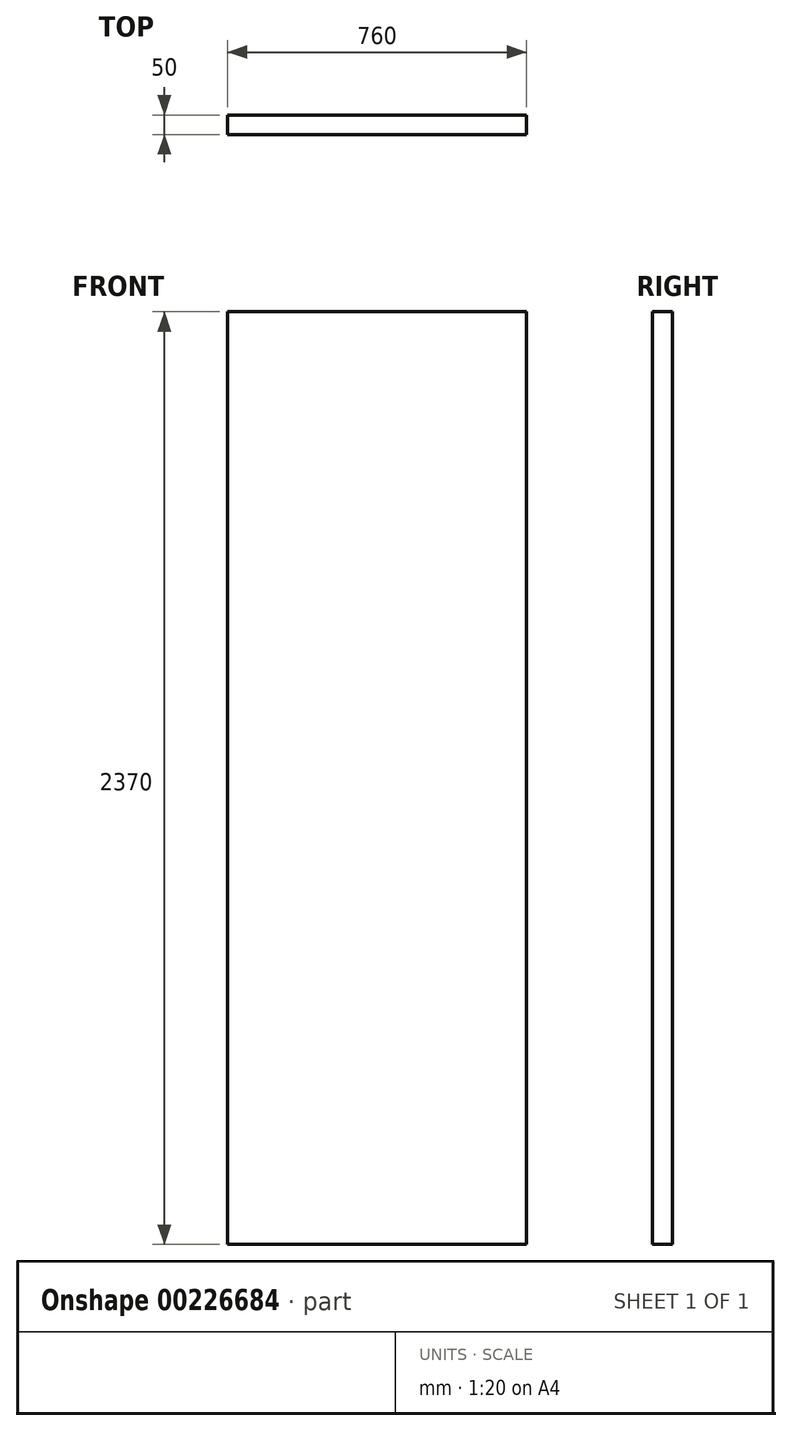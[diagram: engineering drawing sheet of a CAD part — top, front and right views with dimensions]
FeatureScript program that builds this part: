
annotation { "Feature Type Name" : "Feature", "Feature Type Description" : "" }
export const myFeature = defineFeature(function(context is Context, id is Id, definition is map)
    precondition{}
    {
        {
            var Q0;
            Q0=qCreatedBy(makeId("Front.planeOp"),FACE);
            var sketch = newSketch(context, id + "F0", { "sketchPlane" : qUnion([Q0])});
            skLineSegment(sketch, "E0.bottom", {"start": v(-380, 1185) * mm, "end": v(380, 1185) * mm});
            skLineSegment(sketch, "E0.top", {"start": v(-380, -1185) * mm, "end": v(380, -1185) * mm});
            skLineSegment(sketch, "E0.left", {"start": v(-380, 1185) * mm, "end": v(-380, -1185) * mm});
            skLineSegment(sketch, "E0.right", {"start": v(380, 1185) * mm, "end": v(380, -1185) * mm});
            skPoint(sketch, "E0.middle", {"position": v(0, 0) * mm});
            skSolve(sketch);
        }
        {
            var Q0;
            Q0=makeQuery(id+"F0.imprint","IMPRINT",FACE,{"disambiguationData":[TD([[makeQuery(id+"F0.imprint","IMPRINT",EDGE,{"derivedFrom":sQuery(id+"F0.wireOp",EDGE,"E0.bottom")}),-1.0]])]});
            extrude(context, id + "F1", {"entities" : qUnion([Q0]), "depth" : 50 * mm});
        }
    });
